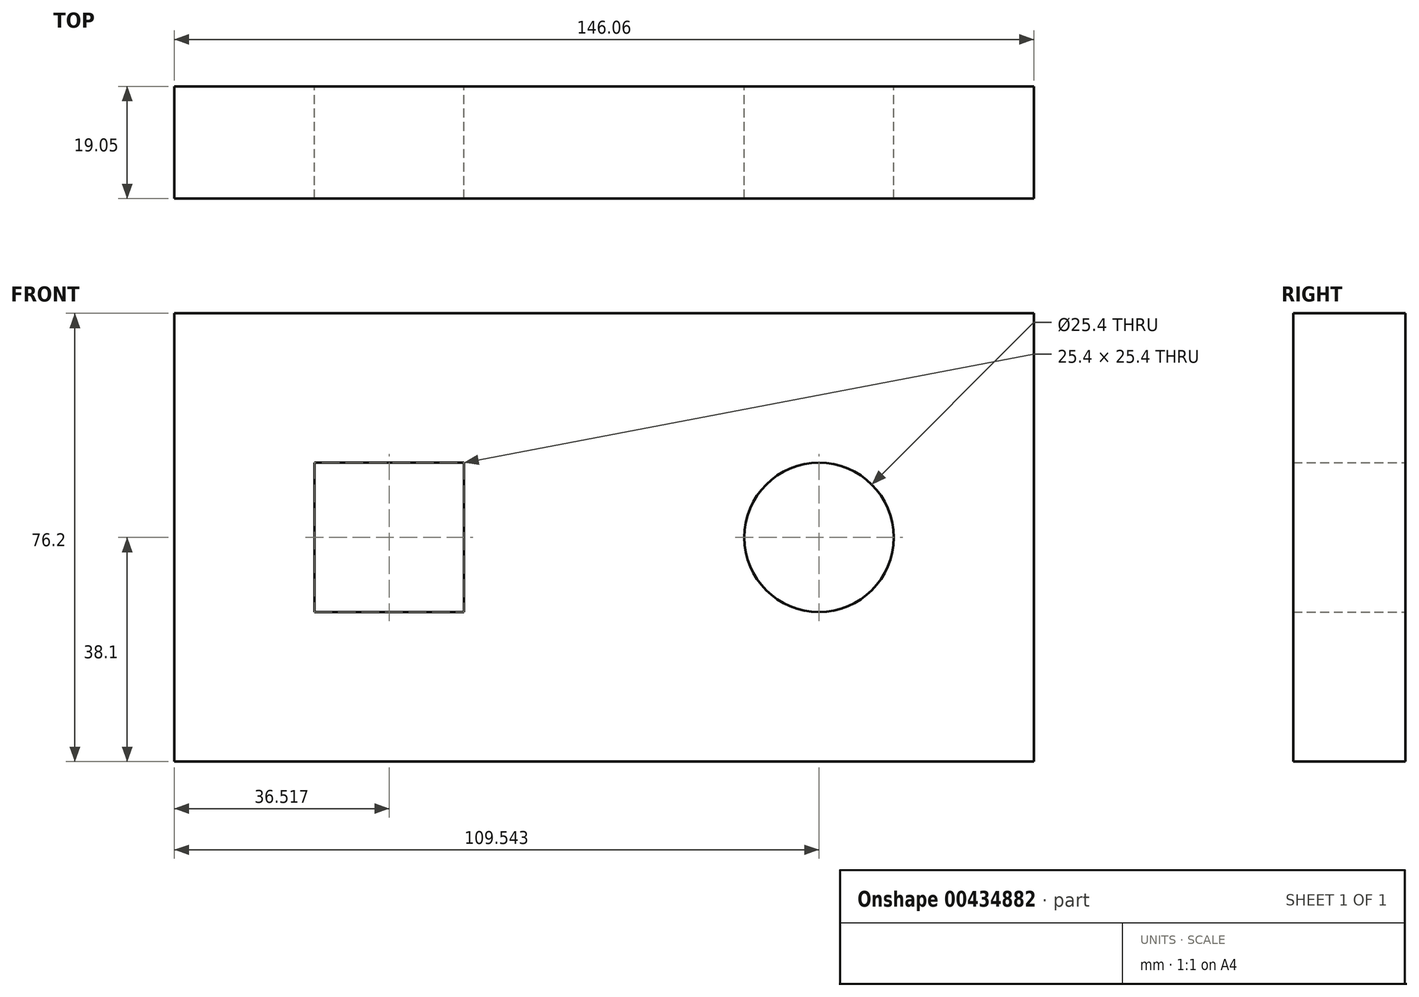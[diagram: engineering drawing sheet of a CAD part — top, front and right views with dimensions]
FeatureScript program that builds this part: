
annotation { "Feature Type Name" : "Feature", "Feature Type Description" : "" }
export const myFeature = defineFeature(function(context is Context, id is Id, definition is map)
    precondition{}
    {
        {
            var Q0;
            Q0=qCreatedBy(makeId("Front.planeOp"),FACE);
            var sketch = newSketch(context, id + "F0", { "sketchPlane" : qUnion([Q0])});
            skLineSegment(sketch, "E0.bottom", {"start": v(73.03, -38.1) * mm, "end": v(-73.03, -38.1) * mm});
            skLineSegment(sketch, "E0.top", {"start": v(73.03, 38.1) * mm, "end": v(-73.03, 38.1) * mm});
            skLineSegment(sketch, "E0.left", {"start": v(73.03, -38.1) * mm, "end": v(73.03, 38.1) * mm});
            skLineSegment(sketch, "E0.right", {"start": v(-73.03, -38.1) * mm, "end": v(-73.03, 38.1) * mm});
            skPoint(sketch, "E0.middle", {"position": v(0, 0) * mm});
            skCircle(sketch, "E1", {"center": v(36.51, 0) * mm, "radius": 12.7 * mm});
            skLineSegment(sketch, "E2.bottom", {"start": v(-49.21, -12.7) * mm, "end": v(-23.81, -12.7) * mm});
            skLineSegment(sketch, "E2.top", {"start": v(-49.21, 12.7) * mm, "end": v(-23.81, 12.7) * mm});
            skLineSegment(sketch, "E2.left", {"start": v(-49.21, -12.7) * mm, "end": v(-49.21, 12.7) * mm});
            skLineSegment(sketch, "E2.right", {"start": v(-23.81, -12.7) * mm, "end": v(-23.81, 12.7) * mm});
            skPoint(sketch, "E2.middle", {"position": v(-36.51, 0) * mm});
            skSolve(sketch);
        }
        {
            var Q0;
            Q0 = qSketchRegion(id + "F0", true);
            extrude(context, id + "F1", {"entities" : qUnion([Q0]), "depth" : 19.05 * mm});
        }
    });
